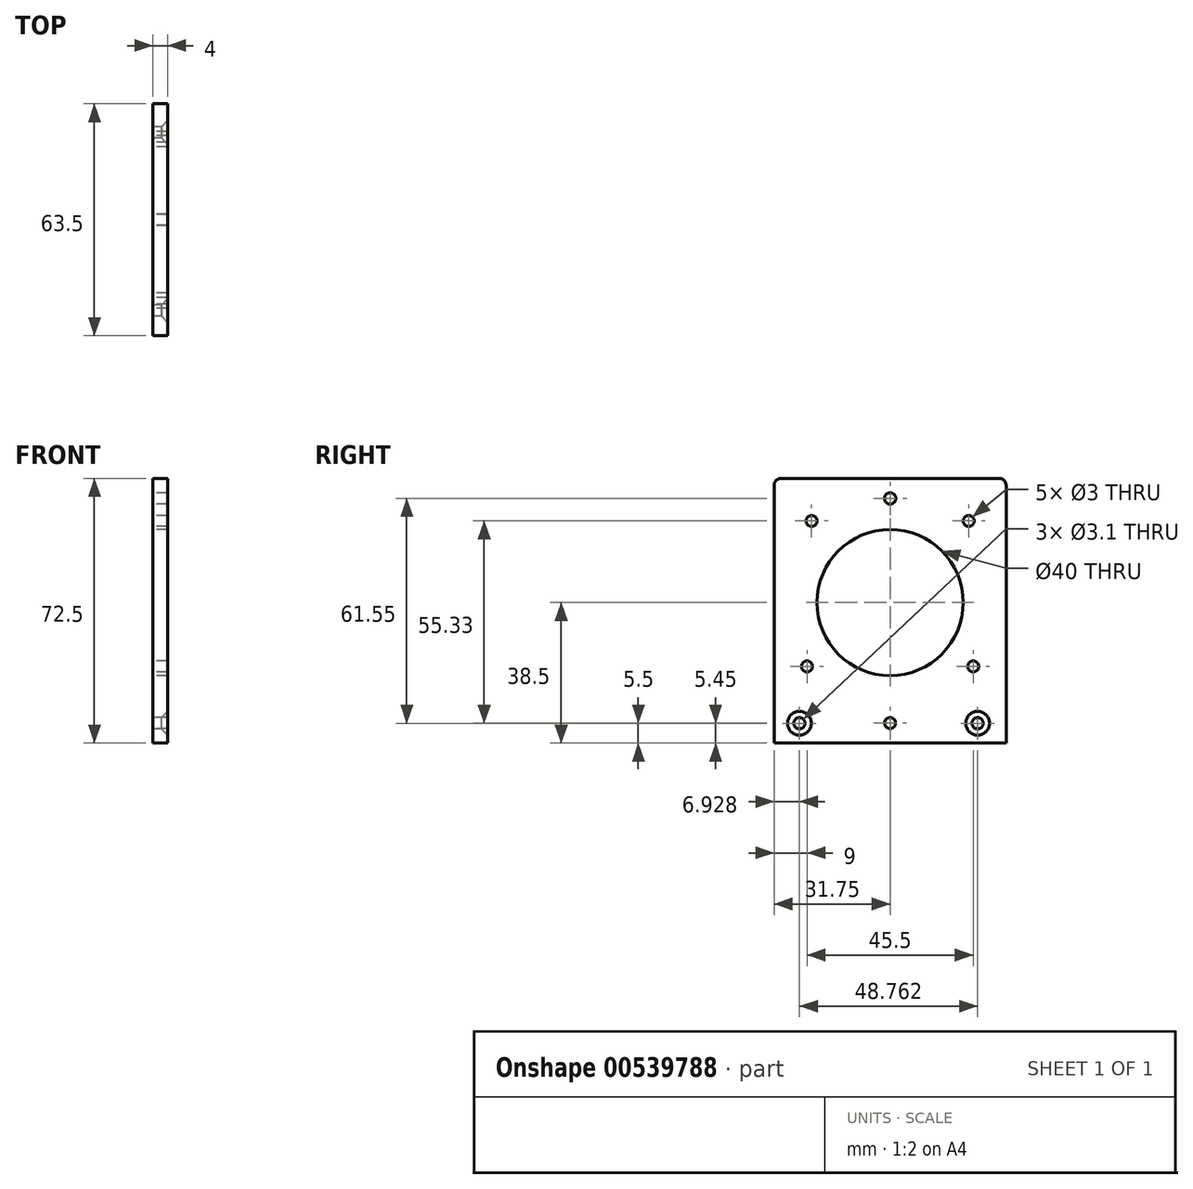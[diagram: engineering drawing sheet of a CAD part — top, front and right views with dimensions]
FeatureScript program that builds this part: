
annotation { "Feature Type Name" : "Feature", "Feature Type Description" : "" }
export const myFeature = defineFeature(function(context is Context, id is Id, definition is map)
    precondition{}
    {
        {
            var Q0;
            Q0=qCreatedBy(makeId("Right.planeOp"),FACE);
            var sketch = newSketch(context, id + "F0", { "sketchPlane" : qUnion([Q0])});
            skLineSegment(sketch, "E0.bottom", {"start": v(29.75, 36.25) * mm, "end": v(-29.75, 36.25) * mm});
            skLineSegment(sketch, "E0.top", {"start": v(31.75, -36.25) * mm, "end": v(-31.75, -36.25) * mm});
            skLineSegment(sketch, "E0.left", {"start": v(31.75, 34.25) * mm, "end": v(31.75, -36.25) * mm});
            skLineSegment(sketch, "E0.right", {"start": v(-31.75, 34.25) * mm, "end": v(-31.75, -36.25) * mm});
            skPoint(sketch, "E0.middle", {"position": v(0, 0) * mm});
            skPoint(sketch, "E1.visualSharp", {"position": v(-31.75, 36.25) * mm});
            skArc(sketch, "E1.filletArc", {"start": v(-29.75, 36.25) * mm, "mid": v(-31.16, 35.66) * mm, "end": v(-31.75, 34.25) * mm});
            skPoint(sketch, "E2.visualSharp", {"position": v(31.75, 36.25) * mm});
            skArc(sketch, "E2.filletArc", {"start": v(31.75, 34.25) * mm, "mid": v(31.16, 35.66) * mm, "end": v(29.75, 36.25) * mm});
            skCircle(sketch, "E3", {"center": v(0, 2.25) * mm, "radius": 20 * mm});
            skCircle(sketch, "E4", {"center": v(-21.5, 24.58) * mm, "radius": 1.5 * mm});
            skCircle(sketch, "E5", {"center": v(21.5, 24.58) * mm, "radius": 1.5 * mm});
            skCircle(sketch, "E6", {"center": v(0, -30.75) * mm, "radius": 1.5 * mm});
            skCircle(sketch, "E7", {"center": v(-24.82, -30.8) * mm, "radius": 1.55 * mm});
            skCircle(sketch, "E8", {"center": v(23.94, -30.8) * mm, "radius": 1.55 * mm});
            skCircle(sketch, "E9", {"center": v(0, 30.75) * mm, "radius": 1.55 * mm});
            skCircle(sketch, "E10", {"center": v(-22.75, -15.25) * mm, "radius": 1.5 * mm});
            skCircle(sketch, "E11", {"center": v(22.75, -15.25) * mm, "radius": 1.5 * mm});
            skSolve(sketch);
        }
        {
            var Q0;
            Q0=qSketchRegion(id+"F0",true);
            extrude(context, id + "F1", {"entities" : qUnion([Q0]), "depth" : 4 * mm, "offsetDistance" : 25 * mm});
        }
        {
            var Q0;
            Q0=makeQuery(id+"F1.opExtrude","CAP_EDGE",EDGE,{"disambiguationData":[OSD([sQuery(id+"F0.wireOp",EDGE,"E7")])],"isStart":false});
            var Q1;
            Q1=makeQuery(id+"F1.opExtrude","CAP_EDGE",EDGE,{"disambiguationData":[OSD([sQuery(id+"F0.wireOp",EDGE,"E8")])],"isStart":false});
            chamfer(context, id + "F2", {"entities" : qUnion([Q0, Q1]), "width" : 1.7 * mm, "tangentPropagation" : true});
        }
    });
